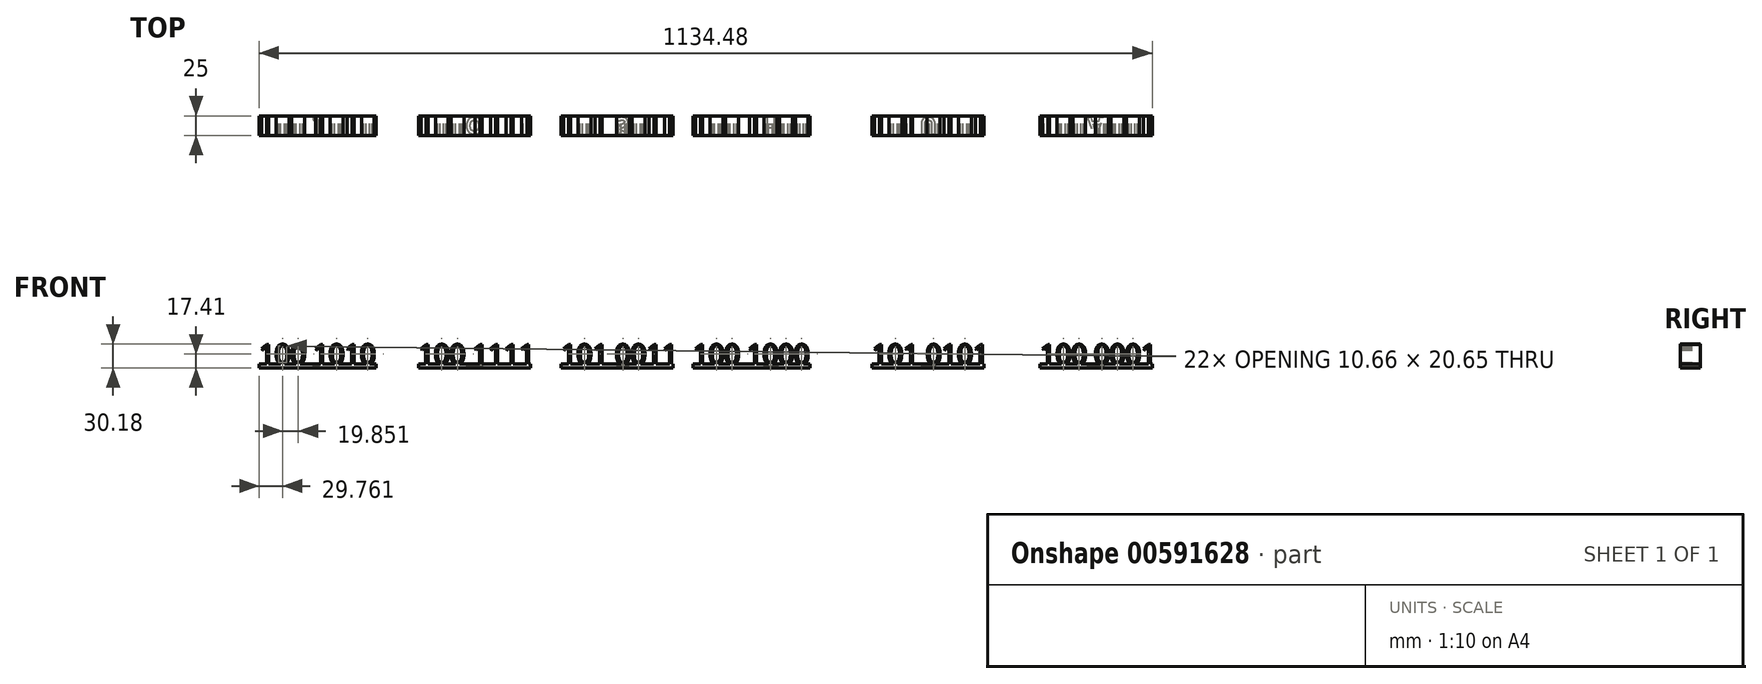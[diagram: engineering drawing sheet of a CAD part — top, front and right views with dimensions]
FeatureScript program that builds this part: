
annotation { "Feature Type Name" : "Feature", "Feature Type Description" : "" }
export const myFeature = defineFeature(function(context is Context, id is Id, definition is map)
    precondition{}
    {
        {
            var Q0;
            Q0=qCreatedBy(makeId("Front.planeOp"),FACE);
            var sketch = newSketch(context, id + "F0", { "sketchPlane" : qUnion([Q0])});
            skText(sketch, "E0", { "text": "100 1010", "fontName": "OpenSans-Regular.ttf"});
            skLineSegment(sketch, "E1.bottom", {"start": v(-153, 0) * mm, "end": v(-4.49, 0) * mm});
            skLineSegment(sketch, "E1.top", {"start": v(-153, -5) * mm, "end": v(-4.49, -5) * mm});
            skLineSegment(sketch, "E1.left", {"start": v(-153, 0) * mm, "end": v(-153, -5) * mm});
            skLineSegment(sketch, "E1.right", {"start": v(-4.49, 0) * mm, "end": v(-4.49, -5) * mm});
            skText(sketch, "E2", { "text": "100 1111", "fontName": "OpenSans-Regular.ttf"});
            skLineSegment(sketch, "E3.bottom", {"start": v(49.25, 0) * mm, "end": v(191.75, 0) * mm});
            skLineSegment(sketch, "E3.top", {"start": v(49.25, -5) * mm, "end": v(191.75, -5) * mm});
            skLineSegment(sketch, "E3.left", {"start": v(49.25, 0) * mm, "end": v(49.25, -5) * mm});
            skLineSegment(sketch, "E3.right", {"start": v(191.75, 0) * mm, "end": v(191.75, -5) * mm});
            skText(sketch, "E4", { "text": "101 0011", "fontName": "OpenSans-Regular.ttf"});
            skLineSegment(sketch, "E5.bottom", {"start": v(230.5, 0) * mm, "end": v(373, 0) * mm});
            skLineSegment(sketch, "E5.top", {"start": v(230.5, -5) * mm, "end": v(373, -5) * mm});
            skLineSegment(sketch, "E5.left", {"start": v(230.5, 0) * mm, "end": v(230.5, -5) * mm});
            skLineSegment(sketch, "E5.right", {"start": v(373, 0) * mm, "end": v(373, -5) * mm});
            skText(sketch, "E6", { "text": "100 1000", "fontName": "OpenSans-Regular.ttf"});
            skLineSegment(sketch, "E7.bottom", {"start": v(398.18, 0) * mm, "end": v(546.68, 0) * mm});
            skLineSegment(sketch, "E7.top", {"start": v(398.18, -5) * mm, "end": v(546.68, -5) * mm});
            skLineSegment(sketch, "E7.left", {"start": v(398.18, 0) * mm, "end": v(398.18, -5) * mm});
            skLineSegment(sketch, "E7.right", {"start": v(546.68, 0) * mm, "end": v(546.68, -5) * mm});
            skText(sketch, "E8", { "text": "101 0101", "fontName": "OpenSans-Regular.ttf"});
            skLineSegment(sketch, "E9.bottom", {"start": v(625.29, 0) * mm, "end": v(767.79, 0) * mm});
            skLineSegment(sketch, "E9.top", {"start": v(625.29, -5) * mm, "end": v(767.79, -5) * mm});
            skLineSegment(sketch, "E9.left", {"start": v(625.29, 0) * mm, "end": v(625.29, -5) * mm});
            skLineSegment(sketch, "E9.right", {"start": v(767.79, 0) * mm, "end": v(767.79, -5) * mm});
            skText(sketch, "E10", { "text": "100 0001", "fontName": "OpenSans-Regular.ttf"});
            skLineSegment(sketch, "E11.bottom", {"start": v(838.98, 0) * mm, "end": v(981.48, 0) * mm});
            skLineSegment(sketch, "E11.top", {"start": v(838.98, -5) * mm, "end": v(981.48, -5) * mm});
            skLineSegment(sketch, "E11.left", {"start": v(838.98, 0) * mm, "end": v(838.98, -5) * mm});
            skLineSegment(sketch, "E11.right", {"start": v(981.48, 0) * mm, "end": v(981.48, -5) * mm});
            const initialGuessF0  = {"E0": [-0.153, 0, 1, 0, 0.025], "E2": [0.04925, 0, 1, 0, 0.025], "E4": [0.2305, 0, 1, 0, 0.025], "E6": [0.39818, 0, 1, 0, 0.025], "E8": [0.62529, 0, 1, 0, 0.025], "E10": [0.83898, 0, 1, 0, 0.025]};
            skSetInitialGuess(sketch, initialGuessF0);
            skSolve(sketch);
        }
        {
            var Q0;
            Q0=makeQuery(id+"F0.imprint","IMPRINT",FACE,{"disambiguationData":[TD([[makeQuery(id+"F0.imprint","IMPRINT",EDGE,{"derivedFrom":sQuery(id+"F0.wireOp",EDGE,"E11.top")}),1.0]])]});
            var Q1;
            Q1=makeQuery(id+"F0.imprint","IMPRINT",FACE,{"disambiguationData":[TD([[makeQuery(id+"F0.imprint","IMPRINT",EDGE,{"derivedFrom":sQuery(id+"F0.wireOp",EDGE,"E3.top")}),1.0]])]});
            var Q2;
            {var subQ0=sQuery(id+"F0.wireOp",EDGE,"E8.sketch_text.stroke-9");Q2=makeQuery(id+"F0.imprint","IMPRINT",FACE,{"disambiguationData":[TD([[makeQuery(id+"F0.imprint","IMPRINT",EDGE,{"derivedFrom":subQ0}),-1.0]])]});}
            var Q3;
            Q3=makeQuery(id+"F0.imprint","IMPRINT",FACE,{"disambiguationData":[TD([[makeQuery(id+"F0.imprint","IMPRINT",EDGE,{"derivedFrom":sQuery(id+"F0.wireOp",EDGE,"E5.top")}),1.0]])]});
            var Q4;
            Q4=makeQuery(id+"F0.imprint","IMPRINT",FACE,{"disambiguationData":[TD([[makeQuery(id+"F0.imprint","IMPRINT",EDGE,{"derivedFrom":sQuery(id+"F0.wireOp",EDGE,"E7.top")}),1.0]])]});
            var Q5;
            Q5=makeQuery(id+"F0.imprint","IMPRINT",FACE,{"disambiguationData":[TD([[makeQuery(id+"F0.imprint","IMPRINT",EDGE,{"derivedFrom":sQuery(id+"F0.wireOp",EDGE,"E9.top")}),1.0]])]});
            var Q6;
            {var subQ5=sQuery(id+"F0.wireOp",EDGE,"E10.sketch_text.stroke-57");Q6=makeQuery(id+"F0.imprint","IMPRINT",FACE,{"disambiguationData":[TD([[makeQuery(id+"F0.imprint","IMPRINT",EDGE,{"derivedFrom":subQ5}),-1.0]])]});}
            var Q7;
            {var subQ0=sQuery(id+"F0.wireOp",EDGE,"E8.sketch_text.stroke-51");Q7=makeQuery(id+"F0.imprint","IMPRINT",FACE,{"disambiguationData":[TD([[makeQuery(id+"F0.imprint","IMPRINT",EDGE,{"derivedFrom":subQ0}),-1.0]])]});}
            var Q8;
            {var subQ0=sQuery(id+"F0.wireOp",EDGE,"E2.sketch_text.stroke-69");Q8=makeQuery(id+"F0.imprint","IMPRINT",FACE,{"disambiguationData":[TD([[makeQuery(id+"F0.imprint","IMPRINT",EDGE,{"derivedFrom":subQ0}),-1.0]])]});}
            var Q9;
            {var subQ0=sQuery(id+"F0.wireOp",EDGE,"E6.sketch_text.stroke-52");var subQ1=sQuery(id+"F0.wireOp",EDGE,"E6.sketch_text.stroke-51");var subQ2=makeQuery(id+"F0.imprint","INTERSECT",VERTEX,{"derivedFrom":[subQ1,subQ0]});Q9=makeQuery(id+"F0.imprint","IMPRINT",FACE,{"disambiguationData":[TD([[makeQuery(id+"F0.imprint","IMPRINT",EDGE,{"disambiguationData":[TD([[subQ2,1.0]])],"derivedFrom":subQ1}),-1.0]])]});}
            var Q10;
            {var subQ0=sQuery(id+"F0.wireOp",EDGE,"E10.sketch_text.stroke-43");var subQ1=sQuery(id+"F0.wireOp",EDGE,"E10.sketch_text.stroke-42");var subQ2=makeQuery(id+"F0.imprint","INTERSECT",VERTEX,{"derivedFrom":[subQ1,subQ0]});Q10=makeQuery(id+"F0.imprint","IMPRINT",FACE,{"disambiguationData":[TD([[makeQuery(id+"F0.imprint","IMPRINT",EDGE,{"disambiguationData":[TD([[subQ2,1.0]])],"derivedFrom":subQ1}),-1.0]])]});}
            var Q11;
            {var subQ5=sQuery(id+"F0.wireOp",EDGE,"E6.sketch_text.stroke-9");Q11=makeQuery(id+"F0.imprint","IMPRINT",FACE,{"disambiguationData":[TD([[makeQuery(id+"F0.imprint","IMPRINT",EDGE,{"derivedFrom":subQ5}),-1.0]])]});}
            var Q12;
            {var subQ0=sQuery(id+"F0.wireOp",EDGE,"E4.sketch_text.stroke-1");Q12=makeQuery(id+"F0.imprint","IMPRINT",FACE,{"disambiguationData":[TD([[makeQuery(id+"F0.imprint","IMPRINT",EDGE,{"derivedFrom":subQ0}),-1.0]])]});}
            var Q13;
            {var subQ0=sQuery(id+"F0.wireOp",EDGE,"E8.sketch_text.stroke-61");var subQ1=sQuery(id+"F0.wireOp",EDGE,"E8.sketch_text.stroke-60");var subQ2=makeQuery(id+"F0.imprint","INTERSECT",VERTEX,{"derivedFrom":[subQ1,subQ0]});Q13=makeQuery(id+"F0.imprint","IMPRINT",FACE,{"disambiguationData":[TD([[makeQuery(id+"F0.imprint","IMPRINT",EDGE,{"disambiguationData":[TD([[subQ2,1.0]])],"derivedFrom":subQ1}),-1.0]])]});}
            var Q14;
            {var subQ0=sQuery(id+"F0.wireOp",EDGE,"E6.sketch_text.stroke-66");Q14=makeQuery(id+"F0.imprint","IMPRINT",FACE,{"disambiguationData":[TD([[makeQuery(id+"F0.imprint","IMPRINT",EDGE,{"derivedFrom":subQ0}),-1.0]])]});}
            var Q15;
            {var subQ0=sQuery(id+"F0.wireOp",EDGE,"E2.sketch_text.stroke-9");Q15=makeQuery(id+"F0.imprint","IMPRINT",FACE,{"disambiguationData":[TD([[makeQuery(id+"F0.imprint","IMPRINT",EDGE,{"derivedFrom":subQ0}),-1.0]])]});}
            var Q16;
            {var subQ5=sQuery(id+"F0.wireOp",EDGE,"E6.sketch_text.stroke-82");Q16=makeQuery(id+"F0.imprint","IMPRINT",FACE,{"disambiguationData":[TD([[makeQuery(id+"F0.imprint","IMPRINT",EDGE,{"derivedFrom":subQ5}),-1.0]])]});}
            var Q17;
            {var subQ5=sQuery(id+"F0.wireOp",EDGE,"E0.sketch_text.stroke-50");Q17=makeQuery(id+"F0.imprint","IMPRINT",FACE,{"disambiguationData":[TD([[makeQuery(id+"F0.imprint","IMPRINT",EDGE,{"derivedFrom":subQ5}),-1.0]])]});}
            var Q18;
            {var subQ0=sQuery(id+"F0.wireOp",EDGE,"E10.sketch_text.stroke-11");var subQ1=sQuery(id+"F0.wireOp",EDGE,"E10.sketch_text.stroke-10");var subQ2=makeQuery(id+"F0.imprint","INTERSECT",VERTEX,{"derivedFrom":[subQ1,subQ0]});Q18=makeQuery(id+"F0.imprint","IMPRINT",FACE,{"disambiguationData":[TD([[makeQuery(id+"F0.imprint","IMPRINT",EDGE,{"disambiguationData":[TD([[subQ2,1.0]])],"derivedFrom":subQ1}),-1.0]])]});}
            var Q19;
            {var subQ5=sQuery(id+"F0.wireOp",EDGE,"E0.sketch_text.stroke-75");Q19=makeQuery(id+"F0.imprint","IMPRINT",FACE,{"disambiguationData":[TD([[makeQuery(id+"F0.imprint","IMPRINT",EDGE,{"derivedFrom":subQ5}),-1.0]])]});}
            var Q20;
            {var subQ0=sQuery(id+"F0.wireOp",EDGE,"E6.sketch_text.stroke-27");var subQ1=sQuery(id+"F0.wireOp",EDGE,"E6.sketch_text.stroke-26");var subQ2=makeQuery(id+"F0.imprint","INTERSECT",VERTEX,{"derivedFrom":[subQ1,subQ0]});Q20=makeQuery(id+"F0.imprint","IMPRINT",FACE,{"disambiguationData":[TD([[makeQuery(id+"F0.imprint","IMPRINT",EDGE,{"disambiguationData":[TD([[subQ2,1.0]])],"derivedFrom":subQ1}),-1.0]])]});}
            var Q21;
            {var subQ0=sQuery(id+"F0.wireOp",EDGE,"E0.sketch_text.stroke-42");Q21=makeQuery(id+"F0.imprint","IMPRINT",FACE,{"disambiguationData":[TD([[makeQuery(id+"F0.imprint","IMPRINT",EDGE,{"derivedFrom":subQ0}),-1.0]])]});}
            var Q22;
            {var subQ0=sQuery(id+"F0.wireOp",EDGE,"E10.sketch_text.stroke-27");var subQ1=sQuery(id+"F0.wireOp",EDGE,"E10.sketch_text.stroke-26");var subQ2=makeQuery(id+"F0.imprint","INTERSECT",VERTEX,{"derivedFrom":[subQ1,subQ0]});Q22=makeQuery(id+"F0.imprint","IMPRINT",FACE,{"disambiguationData":[TD([[makeQuery(id+"F0.imprint","IMPRINT",EDGE,{"disambiguationData":[TD([[subQ2,1.0]])],"derivedFrom":subQ1}),-1.0]])]});}
            var Q23;
            {var subQ0=sQuery(id+"F0.wireOp",EDGE,"E6.sketch_text.stroke-25");Q23=makeQuery(id+"F0.imprint","IMPRINT",FACE,{"disambiguationData":[TD([[makeQuery(id+"F0.imprint","IMPRINT",EDGE,{"derivedFrom":subQ0}),-1.0]])]});}
            var Q24;
            {var subQ0=sQuery(id+"F0.wireOp",EDGE,"E10.sketch_text.stroke-25");Q24=makeQuery(id+"F0.imprint","IMPRINT",FACE,{"disambiguationData":[TD([[makeQuery(id+"F0.imprint","IMPRINT",EDGE,{"derivedFrom":subQ0}),-1.0]])]});}
            var Q25;
            {var subQ0=sQuery(id+"F0.wireOp",EDGE,"E6.sketch_text.stroke-50");Q25=makeQuery(id+"F0.imprint","IMPRINT",FACE,{"disambiguationData":[TD([[makeQuery(id+"F0.imprint","IMPRINT",EDGE,{"derivedFrom":subQ0}),-1.0]])]});}
            var Q26;
            {var subQ0=sQuery(id+"F0.wireOp",EDGE,"E8.sketch_text.stroke-76");Q26=makeQuery(id+"F0.imprint","IMPRINT",FACE,{"disambiguationData":[TD([[makeQuery(id+"F0.imprint","IMPRINT",EDGE,{"derivedFrom":subQ0}),-1.0]])]});}
            var Q27;
            {var subQ0=sQuery(id+"F0.wireOp",EDGE,"E6.sketch_text.stroke-11");var subQ1=sQuery(id+"F0.wireOp",EDGE,"E6.sketch_text.stroke-10");var subQ2=makeQuery(id+"F0.imprint","INTERSECT",VERTEX,{"derivedFrom":[subQ1,subQ0]});Q27=makeQuery(id+"F0.imprint","IMPRINT",FACE,{"disambiguationData":[TD([[makeQuery(id+"F0.imprint","IMPRINT",EDGE,{"disambiguationData":[TD([[subQ2,1.0]])],"derivedFrom":subQ1}),-1.0]])]});}
            var Q28;
            {var subQ0=sQuery(id+"F0.wireOp",EDGE,"E4.sketch_text.stroke-26");Q28=makeQuery(id+"F0.imprint","IMPRINT",FACE,{"disambiguationData":[TD([[makeQuery(id+"F0.imprint","IMPRINT",EDGE,{"derivedFrom":subQ0}),-1.0]])]});}
            var Q29;
            {var subQ0=sQuery(id+"F0.wireOp",EDGE,"E8.sketch_text.stroke-26");Q29=makeQuery(id+"F0.imprint","IMPRINT",FACE,{"disambiguationData":[TD([[makeQuery(id+"F0.imprint","IMPRINT",EDGE,{"derivedFrom":subQ0}),-1.0]])]});}
            var Q30;
            {var subQ0=sQuery(id+"F0.wireOp",EDGE,"E10.sketch_text.stroke-41");Q30=makeQuery(id+"F0.imprint","IMPRINT",FACE,{"disambiguationData":[TD([[makeQuery(id+"F0.imprint","IMPRINT",EDGE,{"derivedFrom":subQ0}),-1.0]])]});}
            var Q31;
            {var subQ0=sQuery(id+"F0.wireOp",EDGE,"E2.sketch_text.stroke-11");var subQ1=sQuery(id+"F0.wireOp",EDGE,"E2.sketch_text.stroke-10");var subQ2=makeQuery(id+"F0.imprint","INTERSECT",VERTEX,{"derivedFrom":[subQ1,subQ0]});Q31=makeQuery(id+"F0.imprint","IMPRINT",FACE,{"disambiguationData":[TD([[makeQuery(id+"F0.imprint","IMPRINT",EDGE,{"disambiguationData":[TD([[subQ2,1.0]])],"derivedFrom":subQ1}),-1.0]])]});}
            var Q32;
            {var subQ0=sQuery(id+"F0.wireOp",EDGE,"E10.sketch_text.stroke-1");Q32=makeQuery(id+"F0.imprint","IMPRINT",FACE,{"disambiguationData":[TD([[makeQuery(id+"F0.imprint","IMPRINT",EDGE,{"derivedFrom":subQ0}),-1.0]])]});}
            var Q33;
            {var subQ0=sQuery(id+"F0.wireOp",EDGE,"E6.sketch_text.stroke-68");var subQ1=sQuery(id+"F0.wireOp",EDGE,"E6.sketch_text.stroke-67");var subQ2=makeQuery(id+"F0.imprint","INTERSECT",VERTEX,{"derivedFrom":[subQ1,subQ0]});Q33=makeQuery(id+"F0.imprint","IMPRINT",FACE,{"disambiguationData":[TD([[makeQuery(id+"F0.imprint","IMPRINT",EDGE,{"disambiguationData":[TD([[subQ2,1.0]])],"derivedFrom":subQ1}),-1.0]])]});}
            var Q34;
            {var subQ0=sQuery(id+"F0.wireOp",EDGE,"E4.sketch_text.stroke-67");Q34=makeQuery(id+"F0.imprint","IMPRINT",FACE,{"disambiguationData":[TD([[makeQuery(id+"F0.imprint","IMPRINT",EDGE,{"derivedFrom":subQ0}),-1.0]])]});}
            var Q35;
            {var subQ0=sQuery(id+"F0.wireOp",EDGE,"E10.sketch_text.stroke-59");var subQ1=sQuery(id+"F0.wireOp",EDGE,"E10.sketch_text.stroke-58");var subQ2=makeQuery(id+"F0.imprint","INTERSECT",VERTEX,{"derivedFrom":[subQ1,subQ0]});Q35=makeQuery(id+"F0.imprint","IMPRINT",FACE,{"disambiguationData":[TD([[makeQuery(id+"F0.imprint","IMPRINT",EDGE,{"disambiguationData":[TD([[subQ2,1.0]])],"derivedFrom":subQ1}),-1.0]])]});}
            var Q36;
            {var subQ0=sQuery(id+"F0.wireOp",EDGE,"E2.sketch_text.stroke-51");Q36=makeQuery(id+"F0.imprint","IMPRINT",FACE,{"disambiguationData":[TD([[makeQuery(id+"F0.imprint","IMPRINT",EDGE,{"derivedFrom":subQ0}),-1.0]])]});}
            var Q37;
            {var subQ0=sQuery(id+"F0.wireOp",EDGE,"E2.sketch_text.stroke-60");Q37=makeQuery(id+"F0.imprint","IMPRINT",FACE,{"disambiguationData":[TD([[makeQuery(id+"F0.imprint","IMPRINT",EDGE,{"derivedFrom":subQ0}),-1.0]])]});}
            var Q38;
            Q38=makeQuery(id+"F0.imprint","IMPRINT",FACE,{"disambiguationData":[TD([[makeQuery(id+"F0.imprint","IMPRINT",EDGE,{"derivedFrom":sQuery(id+"F0.wireOp",EDGE,"E1.top")}),1.0]])]});
            var Q39;
            {var subQ0=sQuery(id+"F0.wireOp",EDGE,"E8.sketch_text.stroke-11");var subQ1=sQuery(id+"F0.wireOp",EDGE,"E8.sketch_text.stroke-10");var subQ2=makeQuery(id+"F0.imprint","INTERSECT",VERTEX,{"derivedFrom":[subQ1,subQ0]});Q39=makeQuery(id+"F0.imprint","IMPRINT",FACE,{"disambiguationData":[TD([[makeQuery(id+"F0.imprint","IMPRINT",EDGE,{"disambiguationData":[TD([[subQ2,1.0]])],"derivedFrom":subQ1}),-1.0]])]});}
            var Q40;
            {var subQ0=sQuery(id+"F0.wireOp",EDGE,"E4.sketch_text.stroke-34");Q40=makeQuery(id+"F0.imprint","IMPRINT",FACE,{"disambiguationData":[TD([[makeQuery(id+"F0.imprint","IMPRINT",EDGE,{"derivedFrom":subQ0}),-1.0]])]});}
            var Q41;
            {var subQ0=sQuery(id+"F0.wireOp",EDGE,"E4.sketch_text.stroke-76");Q41=makeQuery(id+"F0.imprint","IMPRINT",FACE,{"disambiguationData":[TD([[makeQuery(id+"F0.imprint","IMPRINT",EDGE,{"derivedFrom":subQ0}),-1.0]])]});}
            var Q42;
            {var subQ0=sQuery(id+"F0.wireOp",EDGE,"E10.sketch_text.stroke-73");Q42=makeQuery(id+"F0.imprint","IMPRINT",FACE,{"disambiguationData":[TD([[makeQuery(id+"F0.imprint","IMPRINT",EDGE,{"derivedFrom":subQ0}),-1.0]])]});}
            var Q43;
            {var subQ5=sQuery(id+"F0.wireOp",EDGE,"E2.sketch_text.stroke-25");Q43=makeQuery(id+"F0.imprint","IMPRINT",FACE,{"disambiguationData":[TD([[makeQuery(id+"F0.imprint","IMPRINT",EDGE,{"derivedFrom":subQ5}),-1.0]])]});}
            var Q44;
            {var subQ0=sQuery(id+"F0.wireOp",EDGE,"E6.sketch_text.stroke-1");Q44=makeQuery(id+"F0.imprint","IMPRINT",FACE,{"disambiguationData":[TD([[makeQuery(id+"F0.imprint","IMPRINT",EDGE,{"derivedFrom":subQ0}),-1.0]])]});}
            var Q45;
            {var subQ0=sQuery(id+"F0.wireOp",EDGE,"E10.sketch_text.stroke-75");var subQ1=sQuery(id+"F0.wireOp",EDGE,"E10.sketch_text.stroke-74");var subQ2=makeQuery(id+"F0.imprint","INTERSECT",VERTEX,{"derivedFrom":[subQ1,subQ0]});Q45=makeQuery(id+"F0.imprint","IMPRINT",FACE,{"disambiguationData":[TD([[makeQuery(id+"F0.imprint","IMPRINT",EDGE,{"disambiguationData":[TD([[subQ2,1.0]])],"derivedFrom":subQ1}),-1.0]])]});}
            var Q46;
            {var subQ0=sQuery(id+"F0.wireOp",EDGE,"E6.sketch_text.stroke-84");var subQ1=sQuery(id+"F0.wireOp",EDGE,"E6.sketch_text.stroke-83");var subQ2=makeQuery(id+"F0.imprint","INTERSECT",VERTEX,{"derivedFrom":[subQ1,subQ0]});Q46=makeQuery(id+"F0.imprint","IMPRINT",FACE,{"disambiguationData":[TD([[makeQuery(id+"F0.imprint","IMPRINT",EDGE,{"disambiguationData":[TD([[subQ2,1.0]])],"derivedFrom":subQ1}),-1.0]])]});}
            var Q47;
            {var subQ0=sQuery(id+"F0.wireOp",EDGE,"E2.sketch_text.stroke-27");var subQ1=sQuery(id+"F0.wireOp",EDGE,"E2.sketch_text.stroke-26");var subQ2=makeQuery(id+"F0.imprint","INTERSECT",VERTEX,{"derivedFrom":[subQ1,subQ0]});Q47=makeQuery(id+"F0.imprint","IMPRINT",FACE,{"disambiguationData":[TD([[makeQuery(id+"F0.imprint","IMPRINT",EDGE,{"disambiguationData":[TD([[subQ2,1.0]])],"derivedFrom":subQ1}),-1.0]])]});}
            var Q48;
            {var subQ0=sQuery(id+"F0.wireOp",EDGE,"E4.sketch_text.stroke-9");Q48=makeQuery(id+"F0.imprint","IMPRINT",FACE,{"disambiguationData":[TD([[makeQuery(id+"F0.imprint","IMPRINT",EDGE,{"derivedFrom":subQ0}),-1.0]])]});}
            var Q49;
            {var subQ0=sQuery(id+"F0.wireOp",EDGE,"E0.sketch_text.stroke-67");Q49=makeQuery(id+"F0.imprint","IMPRINT",FACE,{"disambiguationData":[TD([[makeQuery(id+"F0.imprint","IMPRINT",EDGE,{"derivedFrom":subQ0}),-1.0]])]});}
            var Q50;
            {var subQ0=sQuery(id+"F0.wireOp",EDGE,"E4.sketch_text.stroke-11");var subQ1=sQuery(id+"F0.wireOp",EDGE,"E4.sketch_text.stroke-10");var subQ2=makeQuery(id+"F0.imprint","INTERSECT",VERTEX,{"derivedFrom":[subQ1,subQ0]});Q50=makeQuery(id+"F0.imprint","IMPRINT",FACE,{"disambiguationData":[TD([[makeQuery(id+"F0.imprint","IMPRINT",EDGE,{"disambiguationData":[TD([[subQ2,1.0]])],"derivedFrom":subQ1}),-1.0]])]});}
            var Q51;
            {var subQ1=sQuery(id+"F0.wireOp",EDGE,"E6.sketch_text.stroke-42");Q51=makeQuery(id+"F0.imprint","IMPRINT",FACE,{"disambiguationData":[TD([[makeQuery(id+"F0.imprint","IMPRINT",EDGE,{"derivedFrom":subQ1}),-1.0]])]});}
            var Q52;
            {var subQ0=sQuery(id+"F0.wireOp",EDGE,"E8.sketch_text.stroke-34");Q52=makeQuery(id+"F0.imprint","IMPRINT",FACE,{"disambiguationData":[TD([[makeQuery(id+"F0.imprint","IMPRINT",EDGE,{"derivedFrom":subQ0}),-1.0]])]});}
            var Q53;
            {var subQ0=sQuery(id+"F0.wireOp",EDGE,"E4.sketch_text.stroke-36");var subQ1=sQuery(id+"F0.wireOp",EDGE,"E4.sketch_text.stroke-35");var subQ2=makeQuery(id+"F0.imprint","INTERSECT",VERTEX,{"derivedFrom":[subQ1,subQ0]});Q53=makeQuery(id+"F0.imprint","IMPRINT",FACE,{"disambiguationData":[TD([[makeQuery(id+"F0.imprint","IMPRINT",EDGE,{"disambiguationData":[TD([[subQ2,1.0]])],"derivedFrom":subQ1}),-1.0]])]});}
            var Q54;
            {var subQ0=sQuery(id+"F0.wireOp",EDGE,"E10.sketch_text.stroke-90");Q54=makeQuery(id+"F0.imprint","IMPRINT",FACE,{"disambiguationData":[TD([[makeQuery(id+"F0.imprint","IMPRINT",EDGE,{"derivedFrom":subQ0}),-1.0]])]});}
            var Q55;
            {var subQ0=sQuery(id+"F0.wireOp",EDGE,"E8.sketch_text.stroke-36");var subQ1=sQuery(id+"F0.wireOp",EDGE,"E8.sketch_text.stroke-35");var subQ2=makeQuery(id+"F0.imprint","INTERSECT",VERTEX,{"derivedFrom":[subQ1,subQ0]});Q55=makeQuery(id+"F0.imprint","IMPRINT",FACE,{"disambiguationData":[TD([[makeQuery(id+"F0.imprint","IMPRINT",EDGE,{"disambiguationData":[TD([[subQ2,1.0]])],"derivedFrom":subQ1}),-1.0]])]});}
            var Q56;
            {var subQ0=sQuery(id+"F0.wireOp",EDGE,"E4.sketch_text.stroke-50");Q56=makeQuery(id+"F0.imprint","IMPRINT",FACE,{"disambiguationData":[TD([[makeQuery(id+"F0.imprint","IMPRINT",EDGE,{"derivedFrom":subQ0}),-1.0]])]});}
            var Q57;
            {var subQ0=sQuery(id+"F0.wireOp",EDGE,"E0.sketch_text.stroke-9");Q57=makeQuery(id+"F0.imprint","IMPRINT",FACE,{"disambiguationData":[TD([[makeQuery(id+"F0.imprint","IMPRINT",EDGE,{"derivedFrom":subQ0}),-1.0]])]});}
            var Q58;
            {var subQ0=sQuery(id+"F0.wireOp",EDGE,"E2.sketch_text.stroke-1");Q58=makeQuery(id+"F0.imprint","IMPRINT",FACE,{"disambiguationData":[TD([[makeQuery(id+"F0.imprint","IMPRINT",EDGE,{"derivedFrom":subQ0}),-1.0]])]});}
            var Q59;
            {var subQ0=sQuery(id+"F0.wireOp",EDGE,"E8.sketch_text.stroke-59");Q59=makeQuery(id+"F0.imprint","IMPRINT",FACE,{"disambiguationData":[TD([[makeQuery(id+"F0.imprint","IMPRINT",EDGE,{"derivedFrom":subQ0}),-1.0]])]});}
            var Q60;
            {var subQ0=sQuery(id+"F0.wireOp",EDGE,"E4.sketch_text.stroke-52");var subQ1=sQuery(id+"F0.wireOp",EDGE,"E4.sketch_text.stroke-51");var subQ2=makeQuery(id+"F0.imprint","INTERSECT",VERTEX,{"derivedFrom":[subQ1,subQ0]});Q60=makeQuery(id+"F0.imprint","IMPRINT",FACE,{"disambiguationData":[TD([[makeQuery(id+"F0.imprint","IMPRINT",EDGE,{"disambiguationData":[TD([[subQ2,1.0]])],"derivedFrom":subQ1}),-1.0]])]});}
            var Q61;
            {var subQ0=sQuery(id+"F0.wireOp",EDGE,"E8.sketch_text.stroke-1");Q61=makeQuery(id+"F0.imprint","IMPRINT",FACE,{"disambiguationData":[TD([[makeQuery(id+"F0.imprint","IMPRINT",EDGE,{"derivedFrom":subQ0}),-1.0]])]});}
            var Q62;
            {var subQ5=sQuery(id+"F0.wireOp",EDGE,"E0.sketch_text.stroke-25");Q62=makeQuery(id+"F0.imprint","IMPRINT",FACE,{"disambiguationData":[TD([[makeQuery(id+"F0.imprint","IMPRINT",EDGE,{"derivedFrom":subQ5}),-1.0]])]});}
            var Q63;
            {var subQ5=sQuery(id+"F0.wireOp",EDGE,"E10.sketch_text.stroke-9");Q63=makeQuery(id+"F0.imprint","IMPRINT",FACE,{"disambiguationData":[TD([[makeQuery(id+"F0.imprint","IMPRINT",EDGE,{"derivedFrom":subQ5}),-1.0]])]});}
            var Q64;
            {var subQ0=sQuery(id+"F0.wireOp",EDGE,"E2.sketch_text.stroke-42");Q64=makeQuery(id+"F0.imprint","IMPRINT",FACE,{"disambiguationData":[TD([[makeQuery(id+"F0.imprint","IMPRINT",EDGE,{"derivedFrom":subQ0}),-1.0]])]});}
            var Q65;
            {var subQ0=sQuery(id+"F0.wireOp",EDGE,"E0.sketch_text.stroke-11");var subQ1=sQuery(id+"F0.wireOp",EDGE,"E0.sketch_text.stroke-10");var subQ2=makeQuery(id+"F0.imprint","INTERSECT",VERTEX,{"derivedFrom":[subQ1,subQ0]});Q65=makeQuery(id+"F0.imprint","IMPRINT",FACE,{"disambiguationData":[TD([[makeQuery(id+"F0.imprint","IMPRINT",EDGE,{"disambiguationData":[TD([[subQ2,1.0]])],"derivedFrom":subQ1}),-1.0]])]});}
            var Q66;
            {var subQ0=sQuery(id+"F0.wireOp",EDGE,"E0.sketch_text.stroke-77");var subQ1=sQuery(id+"F0.wireOp",EDGE,"E0.sketch_text.stroke-76");var subQ2=makeQuery(id+"F0.imprint","INTERSECT",VERTEX,{"derivedFrom":[subQ1,subQ0]});Q66=makeQuery(id+"F0.imprint","IMPRINT",FACE,{"disambiguationData":[TD([[makeQuery(id+"F0.imprint","IMPRINT",EDGE,{"disambiguationData":[TD([[subQ2,1.0]])],"derivedFrom":subQ1}),-1.0]])]});}
            var Q67;
            {var subQ0=sQuery(id+"F0.wireOp",EDGE,"E0.sketch_text.stroke-27");var subQ1=sQuery(id+"F0.wireOp",EDGE,"E0.sketch_text.stroke-26");var subQ2=makeQuery(id+"F0.imprint","INTERSECT",VERTEX,{"derivedFrom":[subQ1,subQ0]});Q67=makeQuery(id+"F0.imprint","IMPRINT",FACE,{"disambiguationData":[TD([[makeQuery(id+"F0.imprint","IMPRINT",EDGE,{"disambiguationData":[TD([[subQ2,1.0]])],"derivedFrom":subQ1}),-1.0]])]});}
            var Q68;
            {var subQ0=sQuery(id+"F0.wireOp",EDGE,"E0.sketch_text.stroke-52");var subQ1=sQuery(id+"F0.wireOp",EDGE,"E0.sketch_text.stroke-51");var subQ2=makeQuery(id+"F0.imprint","INTERSECT",VERTEX,{"derivedFrom":[subQ1,subQ0]});Q68=makeQuery(id+"F0.imprint","IMPRINT",FACE,{"disambiguationData":[TD([[makeQuery(id+"F0.imprint","IMPRINT",EDGE,{"disambiguationData":[TD([[subQ2,1.0]])],"derivedFrom":subQ1}),-1.0]])]});}
            var Q69;
            {var subQ0=sQuery(id+"F0.wireOp",EDGE,"E0.sketch_text.stroke-1");Q69=makeQuery(id+"F0.imprint","IMPRINT",FACE,{"disambiguationData":[TD([[makeQuery(id+"F0.imprint","IMPRINT",EDGE,{"derivedFrom":subQ0}),-1.0]])]});}
            extrude(context, id + "F1", {"entities" : qUnion([Q0, Q1, Q2, Q3, Q4, Q5, Q6, Q7, Q8, Q9, Q10, Q11, Q12, Q13, Q14, Q15, Q16, Q17, Q18, Q19, Q20, Q21, Q22, Q23, Q24, Q25, Q26, Q27, Q28, Q29, Q30, Q31, Q32, Q33, Q34, Q35, Q36, Q37, Q38, Q39, Q40, Q41, Q42, Q43, Q44, Q45, Q46, Q47, Q48, Q49, Q50, Q51, Q52, Q53, Q54, Q55, Q56, Q57, Q58, Q59, Q60, Q61, Q62, Q63, Q64, Q65, Q66, Q67, Q68, Q69]), "depth" : 25 * mm, "offsetDistance" : 25 * mm});
        }
        {
            var Q0;
            Q0=makeQuery(id+"F1.opExtrude","SWEPT_FACE",FACE,{"disambiguationData":[OSD([sQuery(id+"F0.wireOp",EDGE,"E1.top")])]});
            var sketch = newSketch(context, id + "F2", { "sketchPlane" : qUnion([Q0])});
            skLineSegment(sketch, "E12.0", {"start": v(49.25, 25) * mm, "end": v(191.75, 25) * mm});
            skLineSegment(sketch, "E13.0", {"start": v(230.5, 25) * mm, "end": v(373, 25) * mm});
            skLineSegment(sketch, "E14.0.0", {"start": v(398.18, 0) * mm, "end": v(546.68, 0) * mm});
            skLineSegment(sketch, "E14.0.1", {"start": v(546.68, 0) * mm, "end": v(546.68, 25) * mm});
            skLineSegment(sketch, "E14.0.2", {"start": v(546.68, 25) * mm, "end": v(398.18, 25) * mm});
            skLineSegment(sketch, "E14.0.3", {"start": v(398.18, 25) * mm, "end": v(398.18, 0) * mm});
            skLineSegment(sketch, "E15.0.0", {"start": v(625.29, 0) * mm, "end": v(767.79, 0) * mm});
            skLineSegment(sketch, "E15.0.1", {"start": v(767.79, 0) * mm, "end": v(767.79, 25) * mm});
            skLineSegment(sketch, "E15.0.2", {"start": v(767.79, 25) * mm, "end": v(625.29, 25) * mm});
            skLineSegment(sketch, "E15.0.3", {"start": v(625.29, 25) * mm, "end": v(625.29, 0) * mm});
            skLineSegment(sketch, "E16.0.0", {"start": v(838.98, 0) * mm, "end": v(981.48, 0) * mm});
            skLineSegment(sketch, "E16.0.1", {"start": v(981.48, 0) * mm, "end": v(981.48, 25) * mm});
            skLineSegment(sketch, "E16.0.2", {"start": v(981.48, 25) * mm, "end": v(838.98, 25) * mm});
            skLineSegment(sketch, "E16.0.3", {"start": v(838.98, 25) * mm, "end": v(838.98, 0) * mm});
            skText(sketch, "E17", { "text": "O", "fontName": "OpenSans-Bold.ttf"});
            skLineSegment(sketch, "E18", {"start": v(120.5, 23) * mm, "end": v(120.5, 25) * mm, "construction": true});
            skLineSegment(sketch, "E19", {"start": v(120.5, 2) * mm, "end": v(120.5, 0) * mm, "construction": true});
            skText(sketch, "E20", { "text": "S", "fontName": "OpenSans-Bold.ttf"});
            skLineSegment(sketch, "E21", {"start": v(301.75, 23) * mm, "end": v(301.75, 25) * mm, "construction": true});
            skLineSegment(sketch, "E22", {"start": v(301.75, 2) * mm, "end": v(301.75, 0) * mm, "construction": true});
            skPoint(sketch, "E23", {"position": v(120.5, 25) * mm});
            skPoint(sketch, "E24", {"position": v(301.75, 25) * mm});
            skPoint(sketch, "E25", {"position": v(472.43, 25) * mm});
            skPoint(sketch, "E26", {"position": v(696.54, 25) * mm});
            skPoint(sketch, "E27", {"position": v(910.23, 25) * mm});
            skText(sketch, "E28", { "text": "H", "fontName": "OpenSans-Bold.ttf"});
            skLineSegment(sketch, "E29", {"start": v(472.43, 2) * mm, "end": v(472.43, 0) * mm, "construction": true});
            skLineSegment(sketch, "E30", {"start": v(472.43, 23) * mm, "end": v(472.43, 25) * mm, "construction": true});
            skText(sketch, "E31", { "text": "U", "fontName": "OpenSans-Bold.ttf"});
            skLineSegment(sketch, "E32", {"start": v(696.54, 23) * mm, "end": v(696.54, 25) * mm, "construction": true});
            skLineSegment(sketch, "E33", {"start": v(696.54, 2) * mm, "end": v(696.54, 0) * mm, "construction": true});
            skText(sketch, "E34", { "text": "A", "fontName": "OpenSans-Bold.ttf"});
            skLineSegment(sketch, "E35", {"start": v(910.23, 23) * mm, "end": v(910.23, 25) * mm, "construction": true});
            skLineSegment(sketch, "E36", {"start": v(910.23, 2) * mm, "end": v(910.23, 0) * mm, "construction": true});
            skText(sketch, "E37", { "text": "J", "fontName": "OpenSans-Bold.ttf"});
            skLineSegment(sketch, "E38", {"start": v(-78.74, 23) * mm, "end": v(-78.74, 25) * mm});
            skPoint(sketch, "E39", {"position": v(-78.74, 25) * mm});
            const initialGuessF2  = {"E17": [0.1088, 0.002, 1, 0, 0.021], "E20": [0.30045, 0.002, 1, 0, 0.021], "E28": [0.48586, 0.002, 1, 0, 0.021], "E31": [0.6858, 0.002, 1, 0, 0.021], "E34": [0.89922, 0.002, 1, 0, 0.021], "E37": [-0.08297, 0.007, 1, 0, 0.016]};
            skSetInitialGuess(sketch, initialGuessF2);
            skSolve(sketch);
        }
        {
            var Q0;
            Q0=makeQuery(id+"F2.imprint","IMPRINT",FACE,{"disambiguationData":[TD([[makeQuery(id+"F2.imprint","IMPRINT",EDGE,{"derivedFrom":sQuery(id+"F2.wireOp",EDGE,"E37.sketch_text.stroke-0")}),-1.0]])]});
            var Q1;
            Q1=makeQuery(id+"F2.imprint","IMPRINT",FACE,{"disambiguationData":[TD([[makeQuery(id+"F2.imprint","IMPRINT",EDGE,{"derivedFrom":sQuery(id+"F2.wireOp",EDGE,"E17.sketch_text.stroke-0")}),-1.0]])]});
            var Q2;
            Q2=makeQuery(id+"F2.imprint","IMPRINT",FACE,{"disambiguationData":[TD([[makeQuery(id+"F2.imprint","IMPRINT",EDGE,{"derivedFrom":sQuery(id+"F2.wireOp",EDGE,"E20.sketch_text.stroke-0")}),-1.0]])]});
            var Q3;
            Q3=makeQuery(id+"F2.imprint","IMPRINT",FACE,{"disambiguationData":[TD([[makeQuery(id+"F2.imprint","IMPRINT",EDGE,{"derivedFrom":sQuery(id+"F2.wireOp",EDGE,"E28.sketch_text.stroke-0")}),-1.0]])]});
            var Q4;
            Q4=makeQuery(id+"F2.imprint","IMPRINT",FACE,{"disambiguationData":[TD([[makeQuery(id+"F2.imprint","IMPRINT",EDGE,{"derivedFrom":sQuery(id+"F2.wireOp",EDGE,"E31.sketch_text.stroke-0")}),-1.0]])]});
            var Q5;
            Q5=makeQuery(id+"F2.imprint","IMPRINT",FACE,{"disambiguationData":[TD([[makeQuery(id+"F2.imprint","IMPRINT",EDGE,{"derivedFrom":sQuery(id+"F2.wireOp",EDGE,"E34.sketch_text.stroke-0")}),-1.0]])]});
            extrude(context, id + "F3", {"entities" : qUnion([Q0, Q1, Q2, Q3, Q4, Q5]), "operationType" : NewBodyOperationType.REMOVE, "oppositeDirection" : true, "depth" : 3 * mm, "offsetDistance" : 25 * mm});
        }
    });
